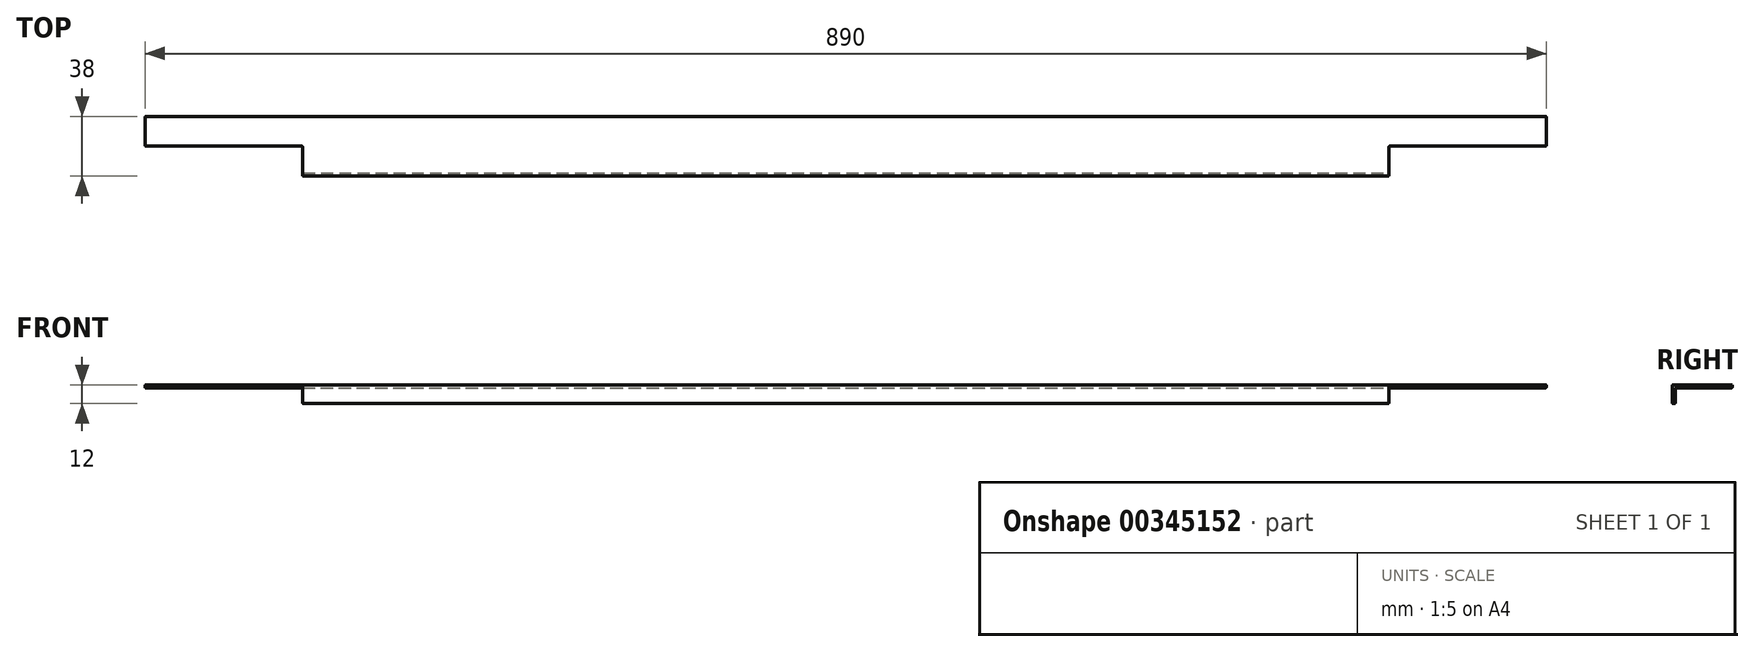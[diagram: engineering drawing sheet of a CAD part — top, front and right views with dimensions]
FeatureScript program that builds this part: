
annotation { "Feature Type Name" : "Feature", "Feature Type Description" : "" }
export const myFeature = defineFeature(function(context is Context, id is Id, definition is map)
    precondition{}
    {
        {
            var Q0;
            Q0=qCreatedBy(makeId("Front.planeOp"),FACE);
            var sketch = newSketch(context, id + "F0", { "sketchPlane" : qUnion([Q0])});
            skLineSegment(sketch, "E0.bottom", {"start": v(0, 0) * mm, "end": v(57.01, 0) * mm});
            skLineSegment(sketch, "E0.top", {"start": v(0, 11.55) * mm, "end": v(57.01, 11.55) * mm});
            skLineSegment(sketch, "E0.left", {"start": v(0, 0) * mm, "end": v(0, 11.55) * mm});
            skLineSegment(sketch, "E0.right", {"start": v(57.01, 0) * mm, "end": v(57.01, 11.55) * mm});
            skSolve(sketch);
        }
        {
            var Q0;
            Q0=makeQuery(id+"F0.imprint","IMPRINT",FACE,{"disambiguationData":[TD([[makeQuery(id+"F0.imprint","IMPRINT",EDGE,{"derivedFrom":sQuery(id+"F0.wireOp",EDGE,"E0.bottom")}),1.0]])]});
            extrude(context, id + "F1", {"entities" : qUnion([Q0]), "depth" : 38 * mm});
        }
        {
            var Q0;
            Q0=makeQuery(id+"F1.opExtrude","SWEPT_FACE",FACE,{"disambiguationData":[OSD([sQuery(id+"F0.wireOp",EDGE,"E0.bottom")])]});
            extrude(context, id + "F2", {"entities" : qUnion([Q0]), "operationType" : NewBodyOperationType.INTERSECT, "oppositeDirection" : true, "depth" : 2 * mm});
        }
        {
            var Q0;
            Q0=makeQuery(id+"F1.opExtrude","SWEPT_FACE",FACE,{"disambiguationData":[OSD([sQuery(id+"F0.wireOp",EDGE,"E0.left")])]});
            extrude(context, id + "F3", {"entities" : qUnion([Q0]), "operationType" : NewBodyOperationType.ADD, "oppositeDirection" : true, "depth" : 890 * mm});
        }
        {
            var Q0;
            Q0=makeQuery(id+"F1.opExtrude","SWEPT_FACE",FACE,{"disambiguationData":[OSD([sQuery(id+"F0.wireOp",EDGE,"E0.left")])]});
            var sketch = newSketch(context, id + "F4", { "sketchPlane" : qUnion([Q0])});
            skLineSegment(sketch, "E1", {"start": v(19, 2) * mm, "end": v(19, 0) * mm});
            skSolve(sketch);
        }
        {
            var Q0;
            {var subQ0=sQuery(id+"F4.wireOp",EDGE,"E1");Q0=makeQuery(id+"F4.imprint","IMPRINT",FACE,{"disambiguationData":[TD([[makeQuery(id+"F4.imprint","IMPRINT",EDGE,{"derivedFrom":subQ0}),1.0]])]});}
            extrude(context, id + "F5", {"entities" : qUnion([Q0]), "operationType" : NewBodyOperationType.REMOVE, "oppositeDirection" : true, "depth" : 100 * mm});
        }
        {
            var Q0;
            Q0=makeQuery(id+"F3.opExtrude","CAP_FACE",FACE,{"disambiguationData":[OSD([sQuery(id+"F0.wireOp",EDGE,"E0.left")])],"isStart":false});
            var sketch = newSketch(context, id + "F6", { "sketchPlane" : qUnion([Q0])});
            skLineSegment(sketch, "E2", {"start": v(-19, 0) * mm, "end": v(-19, 2) * mm});
            skSolve(sketch);
        }
        {
            var Q0;
            {var subQ0=sQuery(id+"F6.wireOp",EDGE,"E2");Q0=makeQuery(id+"F6.imprint","IMPRINT",FACE,{"disambiguationData":[TD([[makeQuery(id+"F6.imprint","IMPRINT",EDGE,{"derivedFrom":subQ0}),1.0]])]});}
            extrude(context, id + "F7", {"entities" : qUnion([Q0]), "operationType" : NewBodyOperationType.REMOVE, "oppositeDirection" : true, "depth" : 100 * mm});
        }
        {
            var Q0;
            {var subQ0=sQuery(id+"F0.wireOp",EDGE,"E0.left");var subQ1=sQuery(id+"F0.wireOp",EDGE,"E0.bottom");Q0=makeQuery(id+"F3.boolean.opBoolean","MERGE",FACE,{"derivedFrom":[makeQuery(id+"F1.opExtrude","SWEPT_FACE",FACE,{"disambiguationData":[OSD([subQ1])]}),makeQuery(id+"F3.opExtrude","SWEPT_FACE",FACE,{"disambiguationData":[OSD([subQ1,subQ0]),TDD([makeQuery(id+"F1.opExtrude","SWEPT_EDGE",EDGE,{"disambiguationData":[OSD([subQ1,subQ0])]})])]})]});}
            var sketch = newSketch(context, id + "F8", { "sketchPlane" : qUnion([Q0])});
            skLineSegment(sketch, "E3.bottom", {"start": v(100, 38) * mm, "end": v(790, 38) * mm});
            skLineSegment(sketch, "E3.top", {"start": v(100, 28.5) * mm, "end": v(790, 28.5) * mm});
            skLineSegment(sketch, "E3.left", {"start": v(100, 38) * mm, "end": v(100, 28.5) * mm});
            skLineSegment(sketch, "E3.right", {"start": v(790, 38) * mm, "end": v(790, 28.5) * mm});
            skSolve(sketch);
        }
        {
            var Q0;
            Q0=makeQuery(id+"F8.imprint","IMPRINT",FACE,{"disambiguationData":[TD([[makeQuery(id+"F8.imprint","IMPRINT",EDGE,{"derivedFrom":sQuery(id+"F8.wireOp",EDGE,"E3.bottom")}),-1.0]])]});
            extrude(context, id + "F9", {"entities" : qUnion([Q0]), "operationType" : NewBodyOperationType.ADD, "depth" : 10 * mm});
        }
        {
            var Q0;
            Q0=makeQuery(id+"F9.opExtrude","SWEPT_FACE",FACE,{"disambiguationData":[OSD([sQuery(id+"F8.wireOp",EDGE,"E3.top")])]});
            extrude(context, id + "F10", {"entities" : qUnion([Q0]), "operationType" : NewBodyOperationType.REMOVE, "oppositeDirection" : true, "depth" : 7.5 * mm});
        }
        {
            var Q0;
            {var subQ0=sQuery(id+"F0.wireOp",EDGE,"E0.left");var subQ1=sQuery(id+"F0.wireOp",EDGE,"E0.bottom");Q0=makeQuery(id+"F3.boolean.opBoolean","MERGE",FACE,{"derivedFrom":[makeQuery(id+"F2.boolean.opBoolean","COPY",FACE,{"derivedFrom":makeQuery(id+"F2.boolean.toolComplement.opBoolean","COPY",FACE,{"derivedFrom":makeQuery(id+"F2.opExtrude","CAP_FACE",FACE,{"disambiguationData":[OSD([subQ1])],"isStart":false})})}),makeQuery(id+"F3.opExtrude","SWEPT_FACE",FACE,{"disambiguationData":[OSD([subQ1,subQ0]),TDD([makeQuery(id+"F2.boolean.opBoolean","COPY",EDGE,{"derivedFrom":makeQuery(id+"F2.boolean.toolComplement.opBoolean","COPY",EDGE,{"derivedFrom":makeQuery(id+"F2.opExtrude","CAP_EDGE",EDGE,{"disambiguationData":[OSD([subQ1,subQ0])],"isStart":false})})})])]})]});}
            var Q1;
            {var subQ0=sQuery(id+"F0.wireOp",EDGE,"E0.left");Q1=makeQuery(id+"F9.boolean.opBoolean","MERGE",FACE,{"derivedFrom":[makeQuery(id+"F3.boolean.opBoolean","MERGE",FACE,{"derivedFrom":[makeQuery(id+"F1.opExtrude","CAP_FACE",FACE,{"disambiguationData":[OSD([sQuery(id+"F0.wireOp",EDGE,"E0.bottom"),sQuery(id+"F0.wireOp",EDGE,"E0.top"),subQ0,sQuery(id+"F0.wireOp",EDGE,"E0.right")])],"isStart":false}),makeQuery(id+"F3.opExtrude","SWEPT_FACE",FACE,{"disambiguationData":[OSD([subQ0]),TDD([makeQuery(id+"F1.opExtrude","CAP_EDGE",EDGE,{"disambiguationData":[OSD([subQ0])],"isStart":false})])]})]}),makeQuery(id+"F9.opExtrude","SWEPT_FACE",FACE,{"disambiguationData":[OSD([sQuery(id+"F8.wireOp",EDGE,"E3.bottom")])]})]});}
            var Q2;
            Q2=makeQuery(id+"F9.boolean.opBoolean","MERGE",FACE,{"derivedFrom":[makeQuery(id+"F5.boolean.opBoolean","COPY",FACE,{"derivedFrom":makeQuery(id+"F5.opExtrude","CAP_FACE",FACE,{"disambiguationData":[OSD([sQuery(id+"F0.wireOp",EDGE,"E0.bottom"),sQuery(id+"F0.wireOp",EDGE,"E0.left"),sQuery(id+"F4.wireOp",EDGE,"E1")])],"isStart":false})}),makeQuery(id+"F9.opExtrude","SWEPT_FACE",FACE,{"disambiguationData":[OSD([sQuery(id+"F8.wireOp",EDGE,"E3.left")])]})]});
            var Q3;
            Q3=makeQuery(id+"F1.opExtrude","SWEPT_FACE",FACE,{"disambiguationData":[OSD([sQuery(id+"F0.wireOp",EDGE,"E0.left")])]});
            var Q4;
            Q4=makeQuery(id+"F5.boolean.opBoolean","COPY",FACE,{"derivedFrom":makeQuery(id+"F5.opExtrude","SWEPT_FACE",FACE,{"disambiguationData":[OSD([sQuery(id+"F4.wireOp",EDGE,"E1")])]})});
            var Q5;
            Q5=makeQuery(id+"F9.boolean.opBoolean","MERGE",FACE,{"derivedFrom":[makeQuery(id+"F7.boolean.opBoolean","COPY",FACE,{"derivedFrom":makeQuery(id+"F7.opExtrude","CAP_FACE",FACE,{"disambiguationData":[OSD([sQuery(id+"F0.wireOp",EDGE,"E0.bottom"),sQuery(id+"F0.wireOp",EDGE,"E0.left"),sQuery(id+"F6.wireOp",EDGE,"E2")])],"isStart":false})}),makeQuery(id+"F9.opExtrude","SWEPT_FACE",FACE,{"disambiguationData":[OSD([sQuery(id+"F8.wireOp",EDGE,"E3.right")])]})]});
            var Q6;
            Q6=makeQuery(id+"F7.boolean.opBoolean","COPY",FACE,{"derivedFrom":makeQuery(id+"F7.opExtrude","SWEPT_FACE",FACE,{"disambiguationData":[OSD([sQuery(id+"F6.wireOp",EDGE,"E2")])]})});
            var Q7;
            Q7=makeQuery(id+"F3.opExtrude","CAP_FACE",FACE,{"disambiguationData":[OSD([sQuery(id+"F0.wireOp",EDGE,"E0.left")])],"isStart":false});
            var Q8;
            {var subQ0=sQuery(id+"F8.wireOp",EDGE,"E3.top");var subQ1=sQuery(id+"F0.wireOp",EDGE,"E0.left");var subQ2=sQuery(id+"F0.wireOp",EDGE,"E0.bottom");Q8=makeQuery(id+"F10.boolean.opBoolean","MERGE",FACE,{"derivedFrom":[makeQuery(id+"F3.boolean.opBoolean","MERGE",FACE,{"derivedFrom":[makeQuery(id+"F1.opExtrude","SWEPT_FACE",FACE,{"disambiguationData":[OSD([subQ2])]}),makeQuery(id+"F3.opExtrude","SWEPT_FACE",FACE,{"disambiguationData":[OSD([subQ2,subQ1]),TDD([makeQuery(id+"F1.opExtrude","SWEPT_EDGE",EDGE,{"disambiguationData":[OSD([subQ2,subQ1])]})])]})]}),makeQuery(id+"F10.opExtrude","SWEPT_FACE",FACE,{"disambiguationData":[OSD([subQ0]),TDD([makeQuery(id+"F9.opExtrude","CAP_EDGE",EDGE,{"disambiguationData":[OSD([subQ0])],"isStart":true})])]})]});}
            fillet(context, id + "F11", {"entities" : qUnion([Q0, Q1, Q2, Q3, Q4, Q5, Q6, Q7, Q8]), "radius" : 0.5 * mm, "tangentPropagation" : true, "allowEdgeOverflow" : false});
        }
        {
            var Q0;
            Q0=makeQuery(id+"F10.boolean.opBoolean","COPY",FACE,{"derivedFrom":makeQuery(id+"F10.opExtrude","CAP_FACE",FACE,{"disambiguationData":[OSD([sQuery(id+"F8.wireOp",EDGE,"E3.top")])],"isStart":false})});
            fillet(context, id + "F12", {"entities" : qUnion([Q0]), "radius" : 0.5 * mm, "tangentPropagation" : true, "allowEdgeOverflow" : false});
        }
    });
